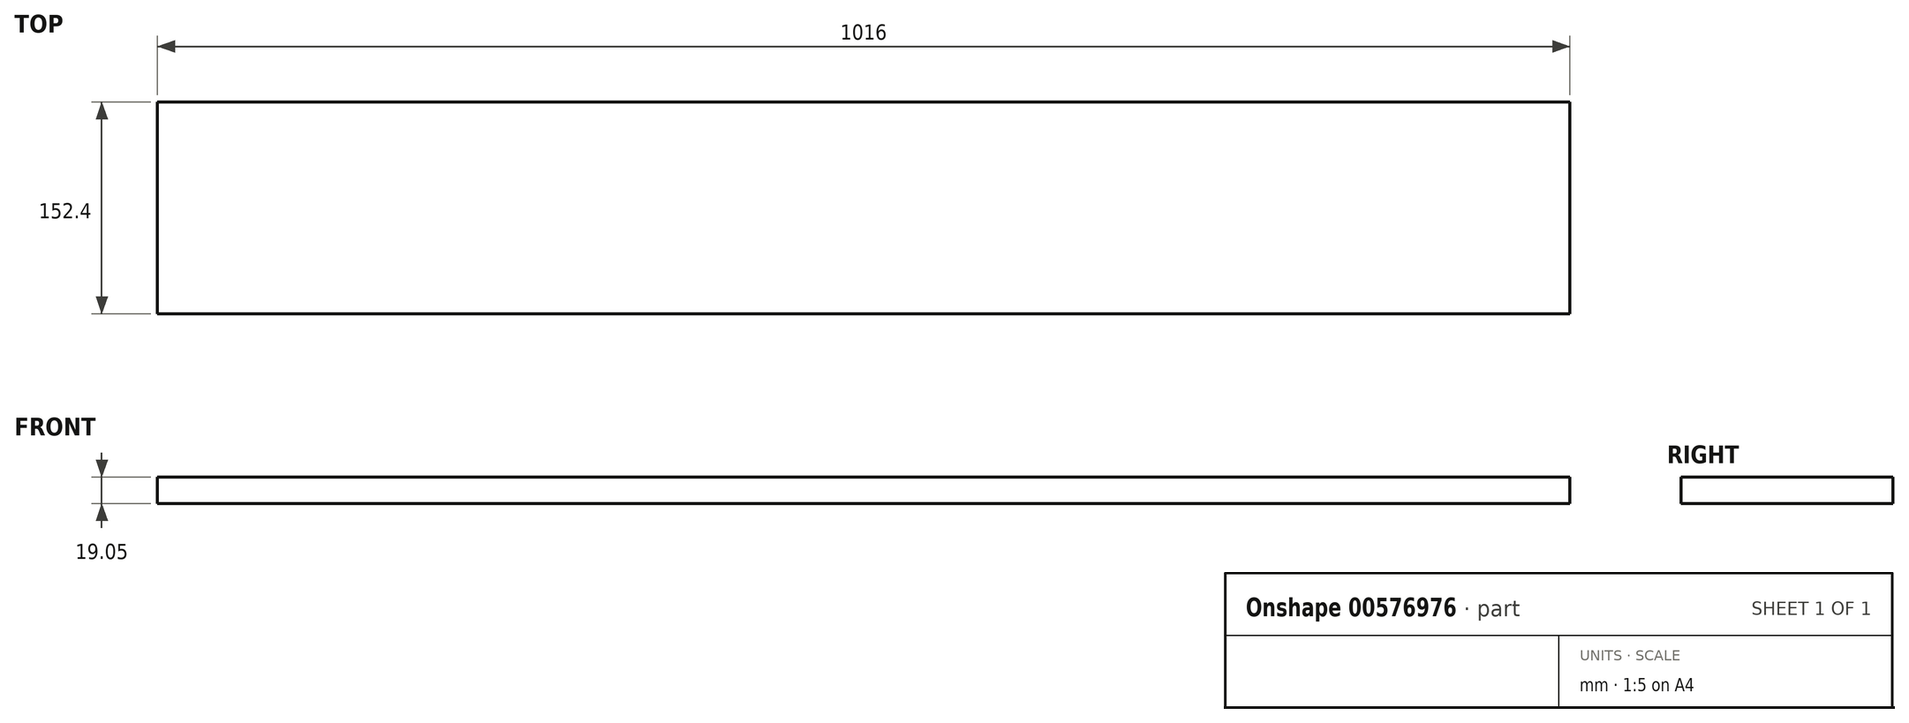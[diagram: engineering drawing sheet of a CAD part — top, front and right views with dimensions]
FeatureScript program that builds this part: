
annotation { "Feature Type Name" : "Feature", "Feature Type Description" : "" }
export const myFeature = defineFeature(function(context is Context, id is Id, definition is map)
    precondition{}
    {
        {
            var Q0;
            Q0=qCreatedBy(makeId("Front.planeOp"),FACE);
            var sketch = newSketch(context, id + "F0", { "sketchPlane" : qUnion([Q0])});
            skLineSegment(sketch, "E0.bottom", {"start": v(-75.95, 0) * mm, "end": v(940.05, 0) * mm});
            skLineSegment(sketch, "E0.top", {"start": v(-75.95, 19.05) * mm, "end": v(940.05, 19.05) * mm});
            skLineSegment(sketch, "E0.left", {"start": v(-75.95, 0) * mm, "end": v(-75.95, 19.05) * mm});
            skLineSegment(sketch, "E0.right", {"start": v(940.05, 0) * mm, "end": v(940.05, 19.05) * mm});
            skSolve(sketch);
        }
        {
            var Q0;
            Q0 = qSketchRegion(id + "F0", true);
            extrude(context, id + "F1", {"entities" : qUnion([Q0]), "oppositeDirection" : true, "depth" : 152.4 * mm, "offsetDistance" : 25.4 * mm});
        }
    });
